annotation { "Feature Type Name" : "Feature", "Feature Type Description" : "" }
export const myFeature = defineFeature(function(context is Context, id is Id, definition is map)
    precondition{}
    {
        {
            var Q0;
            Q0=qCreatedBy(makeId("Front.planeOp"),FACE);
            var sketch = newSketch(context, id + "F0", { "sketchPlane" : qUnion([Q0])});
            skLineSegment(sketch, "E0", {"start": v(0, 0) * mm, "end": v(40, 0) * mm});
            skLineSegment(sketch, "E1", {"start": v(0, 0) * mm, "end": v(21, 45.02) * mm});
            skLineSegment(sketch, "E2.0", {"start": v(7.26, 7.3) * mm, "end": v(24.17, 43.55) * mm});
            skLineSegment(sketch, "E2.1", {"start": v(9.86, 3.5) * mm, "end": v(40, 3.5) * mm});
            skFitSpline(sketch, "E3", {"points": [v(7.26, 7.3) * mm, v(8.57, 5.53) * mm, v(9.86, 3.5) * mm], "startDerivative": vector(-0.72, -2.72) * mm, "endDerivative": vector(3.13, -0.64) * mm});
            skLineSegment(sketch, "E4", {"start": v(40, 0) * mm, "end": v(40, 3.5) * mm});
            skLineSegment(sketch, "E5", {"start": v(21, 45.02) * mm, "end": v(24.17, 43.55) * mm});
            skSolve(sketch);
        }
        {
            var Q0;
            Q0 = qSketchRegion(id + "F0", true);
            extrude(context, id + "F1", {"entities" : qUnion([Q0]), "depth" : 180 * mm, "offsetDistance" : 25 * mm});
        }
        {
            var Q0;
            Q0=makeQuery(id+"F1.opExtrude","SWEPT_FACE",FACE,{"disambiguationData":[OSD([sQuery(id+"F0.wireOp",EDGE,"E1")])]});
            var sketch = newSketch(context, id + "F2", { "sketchPlane" : qUnion([Q0])});
            skText(sketch, "E6", { "text": "Islamic Diet", "fontName": "OpenSans-Bold.ttf"});
            skLineSegment(sketch, "E7.bottom", {"start": v(119.04, 34.05) * mm, "end": v(120.02, 34.05) * mm});
            skLineSegment(sketch, "E7.top", {"start": v(119.04, 31.53) * mm, "end": v(120.02, 31.53) * mm});
            skLineSegment(sketch, "E7.left", {"start": v(119.04, 34.05) * mm, "end": v(119.04, 31.53) * mm});
            skLineSegment(sketch, "E7.right", {"start": v(120.02, 34.05) * mm, "end": v(120.02, 31.53) * mm});
            skLineSegment(sketch, "E8.bottom", {"start": v(96.28, 29.36) * mm, "end": v(97.8, 29.36) * mm});
            skLineSegment(sketch, "E8.top", {"start": v(96.28, 26.24) * mm, "end": v(97.8, 26.24) * mm});
            skLineSegment(sketch, "E8.left", {"start": v(96.28, 29.36) * mm, "end": v(96.28, 26.24) * mm});
            skLineSegment(sketch, "E8.right", {"start": v(97.8, 29.36) * mm, "end": v(97.8, 26.24) * mm});
            skLineSegment(sketch, "E9.bottom", {"start": v(35.2, 28.72) * mm, "end": v(36.45, 28.72) * mm});
            skLineSegment(sketch, "E9.top", {"start": v(35.2, 25.93) * mm, "end": v(36.45, 25.93) * mm});
            skLineSegment(sketch, "E9.left", {"start": v(35.2, 28.72) * mm, "end": v(35.2, 25.93) * mm});
            skLineSegment(sketch, "E9.right", {"start": v(36.45, 28.72) * mm, "end": v(36.45, 25.93) * mm});
            const initialGuessF2  = {"E6": [0.00345, 0.02624, 1, 0, 0.0165]};
            skSetInitialGuess(sketch, initialGuessF2);
            skSolve(sketch);
        }
        {
            var Q0;
            Q0 = qSketchRegion(id + "F2", true);
            extrude(context, id + "F3", {"entities" : qUnion([Q0]), "operationType" : NewBodyOperationType.REMOVE, "oppositeDirection" : true, "depth" : 7 * mm, "offsetDistance" : 25 * mm});
        }
        {
            var Q0;
            {var subQ5=sQuery(id+"F0.wireOp",EDGE,"E1");var subQ6=sQuery(id+"F0.wireOp",EDGE,"E0");Q0=makeQuery(id+"F3.boolean.opBoolean","SPLIT",FACE,{"disambiguationData":[TD([makeQuery(id+"F1.opExtrude","SWEPT_FACE",FACE,{"disambiguationData":[OSD([subQ6])]})])],"derivedFrom":makeQuery(id+"F1.opExtrude","SWEPT_FACE",FACE,{"disambiguationData":[OSD([subQ5])]})});}
            var sketch = newSketch(context, id + "F4", { "sketchPlane" : qUnion([Q0])});
            skCircle(sketch, "E10", {"center": v(160.4, 31.2) * mm, "radius": 16.98 * mm});
            skCircle(sketch, "E11", {"center": v(160.4, 31.2) * mm, "radius": 14.53 * mm});
            skLineSegment(sketch, "E12", {"start": v(149.18, 40.43) * mm, "end": v(169.7, 20.03) * mm});
            skLineSegment(sketch, "E13", {"start": v(167.53, 26.55) * mm, "end": v(155.45, 38.63) * mm});
            skLineSegment(sketch, "E14", {"start": v(155.45, 38.63) * mm, "end": v(151.49, 42.67) * mm});
            skLineSegment(sketch, "E15", {"start": v(167.53, 26.55) * mm, "end": v(171.84, 22.24) * mm});
            skFitSpline(sketch, "E16", {"points": [v(155.45, 38.63) * mm, v(157.23, 39.24) * mm, v(159.16, 39.64) * mm, v(162.09, 39.65) * mm, v(164.5, 39.04) * mm, v(165.52, 38.63) * mm], "startDerivative": vector(9.25, 3.44) * mm, "endDerivative": vector(6.17, -2.65) * mm});
            skFitSpline(sketch, "E17", {"points": [v(165.52, 38.63) * mm, v(166.35, 39.37) * mm, v(166.8, 39.57) * mm, v(167.33, 39.57) * mm, v(167.6, 39.35) * mm, v(167.79, 38.05) * mm, v(168.16, 36.69) * mm], "startDerivative": vector(4.59, 4.44) * mm, "endDerivative": vector(2.04, -5.88) * mm});
            skFitSpline(sketch, "E18", {"points": [v(168.16, 36.69) * mm, v(168.96, 35.8) * mm, v(169.53, 34.8) * mm], "startDerivative": vector(1.7, -1.7) * mm, "endDerivative": vector(1.03, -2.08) * mm});
            skFitSpline(sketch, "E19", {"points": [v(169.53, 34.8) * mm, v(171.58, 34.4) * mm], "startDerivative": vector(2.05, -0.4) * mm, "endDerivative": vector(2.05, -0.4) * mm});
            skFitSpline(sketch, "E20", {"points": [v(171.58, 34.4) * mm, v(171.9, 34.15) * mm, v(171.98, 33.5) * mm, v(172, 29.38) * mm], "startDerivative": vector(2.04, -1.18) * mm, "endDerivative": vector(0.08, -8.5) * mm});
            skFitSpline(sketch, "E21", {"points": [v(172, 29.38) * mm, v(171.82, 29.1) * mm, v(171.52, 28.87) * mm, v(169.32, 28.46) * mm, v(169, 28.1) * mm, v(167.56, 26.51) * mm], "startDerivative": vector(-1.72, -2.39) * mm, "endDerivative": vector(-6.02, -6.18) * mm});
            skFitSpline(sketch, "E22", {"points": [v(152.85, 36.78) * mm, v(152.2, 35.9) * mm], "startDerivative": vector(-0.66, -0.87) * mm, "endDerivative": vector(-0.66, -0.87) * mm});
            skLineSegment(sketch, "E23", {"start": v(152.2, 35.9) * mm, "end": v(151.75, 36.24) * mm});
            skFitSpline(sketch, "E24", {"points": [v(151.75, 36.24) * mm, v(152.09, 36.5) * mm, v(152.29, 36.82) * mm, v(152.42, 37.2) * mm], "startDerivative": vector(1.07, 0.72) * mm, "endDerivative": vector(0.37, 1.18) * mm});
            skFitSpline(sketch, "E25", {"points": [v(151.59, 38.03) * mm, v(151.61, 37.67) * mm, v(151.57, 37.32) * mm, v(151.28, 37.02) * mm], "startDerivative": vector(0.07, -1.1) * mm, "endDerivative": vector(-1.01, -0.8) * mm});
            skFitSpline(sketch, "E26", {"points": [v(151.28, 37.02) * mm, v(150.91, 37.02) * mm, v(150.59, 37.29) * mm, v(150.56, 37.74) * mm, v(150.78, 38.01) * mm, v(151.2, 38.04) * mm, v(151.45, 38.17) * mm], "startDerivative": vector(-2.26, -0.32) * mm, "endDerivative": vector(1.53, 1.17) * mm});
            skFitSpline(sketch, "E27", {"points": [v(150.71, 38.9) * mm, v(150.36, 38.78) * mm, v(150.04, 38.53) * mm, v(149.74, 38.13) * mm, v(149.7, 37.94) * mm, v(149.73, 36.97) * mm], "startDerivative": vector(-2.03, -0.56) * mm, "endDerivative": vector(0.27, -4.04) * mm});
            skLineSegment(sketch, "E28", {"start": v(149.73, 36.97) * mm, "end": v(148.85, 36.84) * mm});
            skFitSpline(sketch, "E29", {"points": [v(148.85, 36.84) * mm, v(148.65, 36.6) * mm, v(148.68, 36.23) * mm, v(148.85, 36.02) * mm, v(150.6, 36.07) * mm], "startDerivative": vector(-1.31, -1.14) * mm, "endDerivative": vector(5.04, 0.54) * mm});
            skLineSegment(sketch, "E30", {"start": v(150.6, 36.07) * mm, "end": v(151.64, 35.1) * mm});
            skFitSpline(sketch, "E31", {"points": [v(151.64, 35.1) * mm, v(151.02, 33.66) * mm, v(150.79, 30.9) * mm, v(151.79, 28.34) * mm, v(153.44, 26.5) * mm, v(154.45, 25.76) * mm], "startDerivative": vector(-3.92, -7.47) * mm, "endDerivative": vector(6.15, -4.1) * mm});
            skLineSegment(sketch, "E32", {"start": v(154.45, 25.76) * mm, "end": v(154.38, 23.61) * mm});
            skFitSpline(sketch, "E33", {"points": [v(154.38, 23.61) * mm, v(154.56, 23.4) * mm, v(155.1, 23.23) * mm, v(158.7, 23.02) * mm, v(159.06, 23.53) * mm, v(159.14, 24.13) * mm], "startDerivative": vector(1.57, -2) * mm, "endDerivative": vector(0.44, 3.65) * mm});
            skLineSegment(sketch, "E34", {"start": v(159.14, 24.13) * mm, "end": v(161.47, 24.13) * mm});
            skLineSegment(sketch, "E35", {"start": v(161.47, 24.13) * mm, "end": v(161.54, 23.34) * mm});
            skFitSpline(sketch, "E36", {"points": [v(161.54, 23.34) * mm, v(161.8, 23.09) * mm, v(163, 22.94) * mm, v(166.65, 23.05) * mm], "startDerivative": vector(1.17, -1.72) * mm, "endDerivative": vector(7.63, 0.32) * mm});
            skCircle(sketch, "E37", {"center": v(166.92, 34.86) * mm, "radius": 0.71 * mm});
            skSolve(sketch);
        }
        {
            var Q0;
            {var subQ3=sQuery(id+"F4.wireOp",EDGE,"E27");Q0=makeQuery(id+"F4.imprint","IMPRINT",FACE,{"disambiguationData":[TD([[makeQuery(id+"F4.imprint","IMPRINT",EDGE,{"derivedFrom":subQ3}),-1.0]])]});}
            var Q1;
            {var subQ4=sQuery(id+"F4.wireOp",EDGE,"E14");Q1=makeQuery(id+"F4.imprint","IMPRINT",FACE,{"disambiguationData":[TD([[makeQuery(id+"F4.imprint","IMPRINT",EDGE,{"derivedFrom":subQ4}),-1.0]])]});}
            var Q2;
            {var subQ0=sQuery(id+"F4.wireOp",EDGE,"E25");Q2=makeQuery(id+"F4.imprint","IMPRINT",FACE,{"disambiguationData":[TD([[makeQuery(id+"F4.imprint","IMPRINT",EDGE,{"derivedFrom":subQ0}),-1.0]])]});}
            var Q3;
            Q3=makeQuery(id+"F4.imprint","IMPRINT",FACE,{"disambiguationData":[TD([[makeQuery(id+"F4.imprint","IMPRINT",EDGE,{"derivedFrom":sQuery(id+"F4.wireOp",EDGE,"E37")}),1.0]])]});
            extrude(context, id + "F5", {"entities" : qUnion([Q0, Q1, Q2, Q3]), "operationType" : NewBodyOperationType.REMOVE, "oppositeDirection" : true, "depth" : 6 * mm, "offsetDistance" : 25 * mm});
        }
        {
            var Q0;
            {var subQ0=sQuery(id+"F2.wireOp",EDGE,"E8.top");var subQ1=sQuery(id+"F2.wireOp",EDGE,"E6.sketch_text.stroke-111");var subQ2=makeQuery(id+"F2.imprint","INTERSECT",VERTEX,{"derivedFrom":[subQ1,subQ0]});Q0=makeQuery(id+"F2.imprint","IMPRINT",FACE,{"disambiguationData":[TD([[makeQuery(id+"F2.imprint","IMPRINT",EDGE,{"disambiguationData":[TD([[subQ2,1.0]])],"derivedFrom":subQ1}),-1.0]])]});}
            var Q1;
            {var subQ0=sQuery(id+"F2.wireOp",EDGE,"E7.left");var subQ1=sQuery(id+"F2.wireOp",EDGE,"E6.sketch_text.stroke-133");var subQ2=makeQuery(id+"F2.imprint","INTERSECT",VERTEX,{"derivedFrom":[subQ1,subQ0]});Q1=makeQuery(id+"F2.imprint","IMPRINT",FACE,{"disambiguationData":[TD([[makeQuery(id+"F2.imprint","IMPRINT",EDGE,{"disambiguationData":[TD([[subQ2,-1.0]])],"derivedFrom":subQ1}),-1.0]])]});}
            var Q2;
            {var subQ1=sQuery(id+"F2.wireOp",EDGE,"E6.sketch_text.stroke-37");var subQ7=sQuery(id+"F2.wireOp",EDGE,"E9.right");var subQ9=makeQuery(id+"F2.imprint","INTERSECT",VERTEX,{"derivedFrom":[subQ1,subQ7]});Q2=makeQuery(id+"F2.imprint","IMPRINT",FACE,{"disambiguationData":[TD([[makeQuery(id+"F2.imprint","IMPRINT",EDGE,{"disambiguationData":[TD([[subQ9,-1.0]])],"derivedFrom":subQ1}),-1.0]])]});}
            extrude(context, id + "F6", {"entities" : qUnion([Q0, Q1, Q2]), "oppositeDirection" : true, "depth" : 3.5 * mm, "offsetDistance" : 25 * mm});
        }
    });